# Revit family: Drinking_Fountain-Haws_Corporation-Wall_Mounted_1001MS
name_source: partatom
category: Plumbing Fixtures
revit_build: Autodesk Revit 2016 (Build: 20150220_1215(x64)
units: mm (PartAtom-declared; Revit-internal decimal feet)

## family parameters
Always vertical = Yes
Cut with Voids When Loaded = No
Host = Wall
OmniClass Number = 23.65.70.14.11
OmniClass Title = Drinking Fountains/Coolers
Part Type = Normal
Room Calculation Point = No
Round Connector Dimension = Use Radius
Shared = Yes

## types (6) — shared parameters
Assembly Code = D2010810
Bowl Diameter = 14 1/8"
Cost = $0
Cost Note = For Cost information please visit the Resource tab in the Product Page URL
Flow = 0.00 GPM
HW Connection = No
Keynote = 15410.A1
Manufacturer = Haws Corporation 1455 Kleppe Lane Sparks, NV 89431
Product Documentation Link = http://www.hawsco.com
Product Page URL = http://www.hawsco.com
Product data url = https://bimobject.com
Sanitary Radius = 5/8"
Series = The Haws 1001 barrier-free drinking fountain
Supply Radius = 3/16"
Tubing = Metal - Haws Corporation - Copper
URL = http://www.hawsco.com
Vent Connection = Yes
Waste Level = 28 3/32"

## per-type parameters (varying)
| type | Back Plate Finish | Bowl Finish | Bracket Finish | CW Connection | CWFU | Description | Pipe Offset | Type Comments | Waste Connection |
| 1001 | Metal - Haws Corporation - Satin Stainless Steel | Metal - Haws Corporation - Satin Stainless Steel | Metal - Haws Corporation - Satin Stainless Steel | No | 1 | Wall Mounted Drinking Fountain with backwall access of plumbing | 12 1/2" | No supplied back panel | No |
| 1001BP | Metal - Haws Corporation - Satin Stainless Steel | Metal - Haws Corporation - Satin Stainless Steel | Metal - Haws Corporation - Satin Stainless Steel | Yes | 2 | Wall Mounted Drinking Fountain with backwall access of plumbing | 12 1/2" | Design with supplied back panel | No |
| 1001HPS | Metal - Haws Corporation - High Polished Stainless Steel | Metal - Haws Corporation - High Polished Stainless Steel | Metal - Haws Corporation - High Polished Stainless Steel | No | 1 | Wall Mounted Drinking Fountain with backwall access of plumbing | 12 1/2" | Design with a high-polished stainless steel finish | No |
| 1001HPSBP | Metal - Haws Corporation - High Polished Stainless Steel | Metal - Haws Corporation - High Polished Stainless Steel | Metal - Haws Corporation - High Polished Stainless Steel | Yes | 2 | Wall Mounted Drinking Fountain with backwall access of plumbing | 12 1/2" | Design with a high-polished stainless steel finish and back panel | No |
| 1001HPSMS | Metal - Haws Corporation - High Polished Stainless Steel | Metal - Haws Corporation - High Polished Stainless Steel | Metal - Haws Corporation - High Polished Stainless Steel | Yes | 3 | Wall Mounted Drinking Fountain with front access of plumbing | 3" | Design with a high-polished stainless steel finish and front access of plumbing | Yes |
| 1001MS | Metal - Haws Corporation - Satin Stainless Steel | Metal - Haws Corporation - Satin Stainless Steel | Metal - Haws Corporation - Satin Stainless Steel | Yes | 3 | Wall Mounted Drinking Fountain with front access of plumbing | 3" | MS (mounting system) allows for front access of plumbing | Yes |

note: column(s) folded — value = type name in every type: Model

## geometry (parser evidence)
native form markers: Blend x34, Sweep x2
no freeform markers — native parametric forms only
